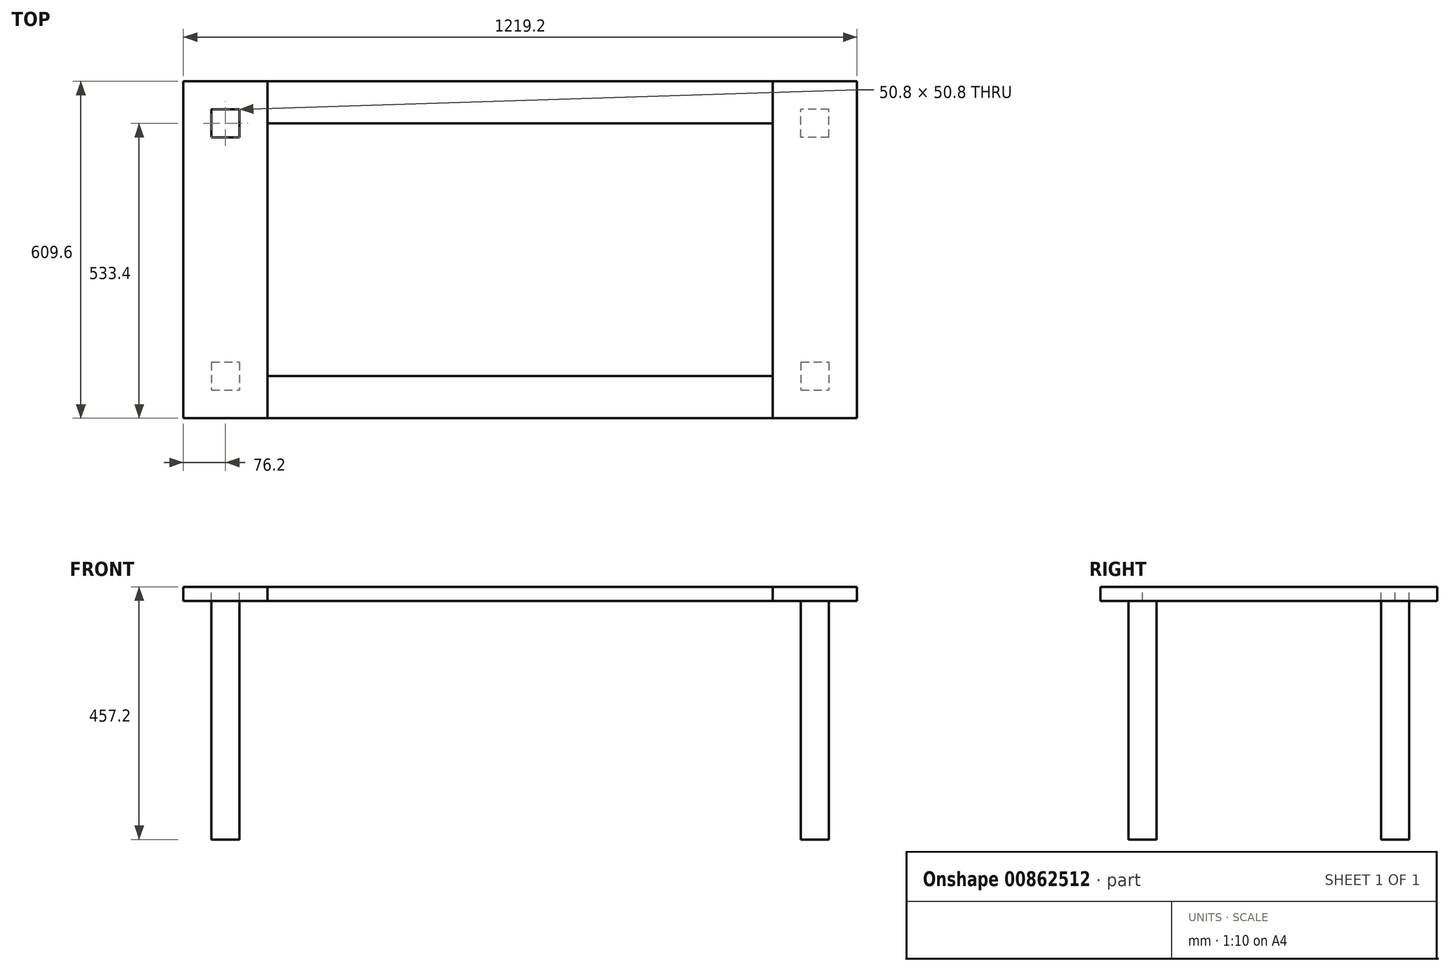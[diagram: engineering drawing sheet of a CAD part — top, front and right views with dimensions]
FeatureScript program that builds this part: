
annotation { "Feature Type Name" : "Feature", "Feature Type Description" : "" }
export const myFeature = defineFeature(function(context is Context, id is Id, definition is map)
    precondition{}
    {
        {
            var Q0;
            Q0=qCreatedBy(makeId("Top.planeOp"),FACE);
            var sketch = newSketch(context, id + "F0", { "sketchPlane" : qUnion([Q0])});
            skLineSegment(sketch, "E0.bottom", {"start": v(-457.2, 228.6) * mm, "end": v(457.2, 228.6) * mm});
            skLineSegment(sketch, "E0.top", {"start": v(-457.2, -228.6) * mm, "end": v(457.2, -228.6) * mm});
            skLineSegment(sketch, "E0.left", {"start": v(-457.2, 228.6) * mm, "end": v(-457.2, -228.6) * mm});
            skLineSegment(sketch, "E0.right", {"start": v(457.2, 228.6) * mm, "end": v(457.2, -228.6) * mm});
            skPoint(sketch, "E0.middle", {"position": v(0, 0) * mm});
            skLineSegment(sketch, "E1.top", {"start": v(-457.2, -304.8) * mm, "end": v(457.2, -304.8) * mm});
            skLineSegment(sketch, "E1.left", {"start": v(-457.2, -228.6) * mm, "end": v(-457.2, -304.8) * mm});
            skLineSegment(sketch, "E1.right", {"start": v(457.2, -228.6) * mm, "end": v(457.2, -304.8) * mm});
            skLineSegment(sketch, "E2.top", {"start": v(-457.2, 304.8) * mm, "end": v(457.2, 304.8) * mm});
            skLineSegment(sketch, "E2.left", {"start": v(-457.2, 228.6) * mm, "end": v(-457.2, 304.8) * mm});
            skLineSegment(sketch, "E2.right", {"start": v(457.2, 228.6) * mm, "end": v(457.2, 304.8) * mm});
            skLineSegment(sketch, "E3.bottom", {"start": v(-457.2, 304.8) * mm, "end": v(-609.6, 304.8) * mm});
            skLineSegment(sketch, "E3.top", {"start": v(-457.2, -304.8) * mm, "end": v(-609.6, -304.8) * mm});
            skLineSegment(sketch, "E3.left", {"start": v(-457.2, 304.8) * mm, "end": v(-457.2, -304.8) * mm});
            skLineSegment(sketch, "E3.right", {"start": v(-609.6, 304.8) * mm, "end": v(-609.6, -304.8) * mm});
            skLineSegment(sketch, "E4.bottom", {"start": v(457.2, 304.8) * mm, "end": v(609.6, 304.8) * mm});
            skLineSegment(sketch, "E4.top", {"start": v(457.2, -304.8) * mm, "end": v(609.6, -304.8) * mm});
            skLineSegment(sketch, "E4.left", {"start": v(457.2, 304.8) * mm, "end": v(457.2, -304.8) * mm});
            skLineSegment(sketch, "E4.right", {"start": v(609.6, 304.8) * mm, "end": v(609.6, -304.8) * mm});
            skLineSegment(sketch, "E5.bottom", {"start": v(-558.8, 254) * mm, "end": v(-508, 254) * mm});
            skLineSegment(sketch, "E5.top", {"start": v(-558.8, 203.2) * mm, "end": v(-508, 203.2) * mm});
            skLineSegment(sketch, "E5.left", {"start": v(-558.8, 254) * mm, "end": v(-558.8, 203.2) * mm});
            skLineSegment(sketch, "E5.right", {"start": v(-508, 254) * mm, "end": v(-508, 203.2) * mm});
            skPoint(sketch, "E5.middle", {"position": v(-533.4, 228.6) * mm});
            skPoint(sketch, "E5.middle.positionSnap0", {"position": v(-533.4, 304.8) * mm});
            skPoint(sketch, "E5.centerSnap0", {"position": v(-533.4, 304.8) * mm});
            skLineSegment(sketch, "E6.bottom", {"start": v(-558.8, -203.2) * mm, "end": v(-508, -203.2) * mm});
            skLineSegment(sketch, "E6.top", {"start": v(-558.8, -254) * mm, "end": v(-508, -254) * mm});
            skLineSegment(sketch, "E6.left", {"start": v(-558.8, -203.2) * mm, "end": v(-558.8, -254) * mm});
            skLineSegment(sketch, "E6.right", {"start": v(-508, -203.2) * mm, "end": v(-508, -254) * mm});
            skPoint(sketch, "E6.middle", {"position": v(-533.4, -228.6) * mm});
            skPoint(sketch, "E6.middle.positionSnap0", {"position": v(-533.4, -304.8) * mm});
            skPoint(sketch, "E6.centerSnap0", {"position": v(-533.4, -304.8) * mm});
            skLineSegment(sketch, "E7.bottom", {"start": v(558.8, 203.2) * mm, "end": v(508, 203.2) * mm});
            skLineSegment(sketch, "E7.top", {"start": v(558.8, 254) * mm, "end": v(508, 254) * mm});
            skLineSegment(sketch, "E7.left", {"start": v(558.8, 203.2) * mm, "end": v(558.8, 254) * mm});
            skLineSegment(sketch, "E7.right", {"start": v(508, 203.2) * mm, "end": v(508, 254) * mm});
            skPoint(sketch, "E7.middle", {"position": v(533.4, 228.6) * mm});
            skPoint(sketch, "E7.middle.positionSnap0", {"position": v(533.4, 304.8) * mm});
            skPoint(sketch, "E7.centerSnap0", {"position": v(533.4, 304.8) * mm});
            skLineSegment(sketch, "E8.bottom", {"start": v(508, -203.2) * mm, "end": v(558.8, -203.2) * mm});
            skLineSegment(sketch, "E8.top", {"start": v(508, -254) * mm, "end": v(558.8, -254) * mm});
            skLineSegment(sketch, "E8.left", {"start": v(508, -203.2) * mm, "end": v(508, -254) * mm});
            skLineSegment(sketch, "E8.right", {"start": v(558.8, -203.2) * mm, "end": v(558.8, -254) * mm});
            skPoint(sketch, "E8.middle", {"position": v(533.4, -228.6) * mm});
            skPoint(sketch, "E8.middle.positionSnap0", {"position": v(533.4, -304.8) * mm});
            skPoint(sketch, "E8.centerSnap0", {"position": v(533.4, -304.8) * mm});
            skSolve(sketch);
        }
        {
            var Q0;
            Q0=makeQuery(id+"F0.imprint","IMPRINT",FACE,{"disambiguationData":[TD([[makeQuery(id+"F0.imprint","IMPRINT",EDGE,{"derivedFrom":sQuery(id+"F0.wireOp",EDGE,"E0.left")}),-1.0]])]});
            var sketch = newSketch(context, id + "F1", { "sketchPlane" : qUnion([Q0])});
            skSolve(sketch);
        }
        {
            var Q0;
            Q0=makeQuery(id+"F1.imprint","IMPRINT",FACE,{"disambiguationData":[TD([[makeQuery(id+"F1.imprint","IMPRINT",EDGE,{"derivedFrom":makeQuery(id+"F0.imprint","IMPRINT",EDGE,{"derivedFrom":sQuery(id+"F0.wireOp",EDGE,"E0.left")})}),-1.0]])]});
            extrude(context, id + "F2", {"entities" : qUnion([Q0]), "oppositeDirection" : true, "depth" : 25.4 * mm, "offsetDistance" : 25.4 * mm});
        }
        {
            var Q0;
            Q0=makeQuery(id+"F0.imprint","IMPRINT",FACE,{"disambiguationData":[TD([[makeQuery(id+"F0.imprint","IMPRINT",EDGE,{"derivedFrom":sQuery(id+"F0.wireOp",EDGE,"E0.right")}),1.0]])]});
            extrude(context, id + "F3", {"entities" : qUnion([Q0]), "oppositeDirection" : true, "depth" : 25.4 * mm, "offsetDistance" : 25.4 * mm});
        }
        {
            var Q0;
            Q0=makeQuery(id+"F0.imprint","IMPRINT",FACE,{"disambiguationData":[TD([[makeQuery(id+"F0.imprint","IMPRINT",EDGE,{"derivedFrom":sQuery(id+"F0.wireOp",EDGE,"E0.bottom")}),1.0]])]});
            extrude(context, id + "F4", {"entities" : qUnion([Q0]), "oppositeDirection" : true, "depth" : 25.4 * mm, "offsetDistance" : 25.4 * mm});
        }
        {
            var Q0;
            Q0=makeQuery(id+"F0.imprint","IMPRINT",FACE,{"disambiguationData":[TD([[makeQuery(id+"F0.imprint","IMPRINT",EDGE,{"derivedFrom":sQuery(id+"F0.wireOp",EDGE,"E0.top")}),-1.0]])]});
            extrude(context, id + "F5", {"entities" : qUnion([Q0]), "oppositeDirection" : true, "depth" : 25.4 * mm, "offsetDistance" : 25.4 * mm});
        }
        {
            var Q0;
            Q0=makeQuery(id+"F0.imprint","IMPRINT",FACE,{"disambiguationData":[TD([[makeQuery(id+"F0.imprint","IMPRINT",EDGE,{"derivedFrom":sQuery(id+"F0.wireOp",EDGE,"E5.bottom")}),-1.0]])]});
            extrude(context, id + "F6", {"entities" : qUnion([Q0]), "oppositeDirection" : true, "depth" : 457.2 * mm, "offsetDistance" : 25.4 * mm});
        }
        {
            var Q0;
            Q0=makeQuery(id+"F0.imprint","IMPRINT",FACE,{"disambiguationData":[TD([[makeQuery(id+"F0.imprint","IMPRINT",EDGE,{"derivedFrom":sQuery(id+"F0.wireOp",EDGE,"E6.bottom")}),-1.0]])]});
            extrude(context, id + "F7", {"entities" : qUnion([Q0]), "operationType" : NewBodyOperationType.ADD, "oppositeDirection" : true, "depth" : 457.2 * mm, "offsetDistance" : 25.4 * mm});
        }
        {
            var Q0;
            Q0=makeQuery(id+"F0.imprint","IMPRINT",FACE,{"disambiguationData":[TD([[makeQuery(id+"F0.imprint","IMPRINT",EDGE,{"derivedFrom":sQuery(id+"F0.wireOp",EDGE,"E8.bottom")}),-1.0]])]});
            extrude(context, id + "F8", {"entities" : qUnion([Q0]), "operationType" : NewBodyOperationType.ADD, "oppositeDirection" : true, "depth" : 457.2 * mm, "offsetDistance" : 25.4 * mm});
        }
        {
            var Q0;
            Q0=makeQuery(id+"F0.imprint","IMPRINT",FACE,{"disambiguationData":[TD([[makeQuery(id+"F0.imprint","IMPRINT",EDGE,{"derivedFrom":sQuery(id+"F0.wireOp",EDGE,"E7.bottom")}),-1.0]])]});
            extrude(context, id + "F9", {"entities" : qUnion([Q0]), "operationType" : NewBodyOperationType.ADD, "oppositeDirection" : true, "depth" : 457.2 * mm, "offsetDistance" : 25.4 * mm});
        }
    });
